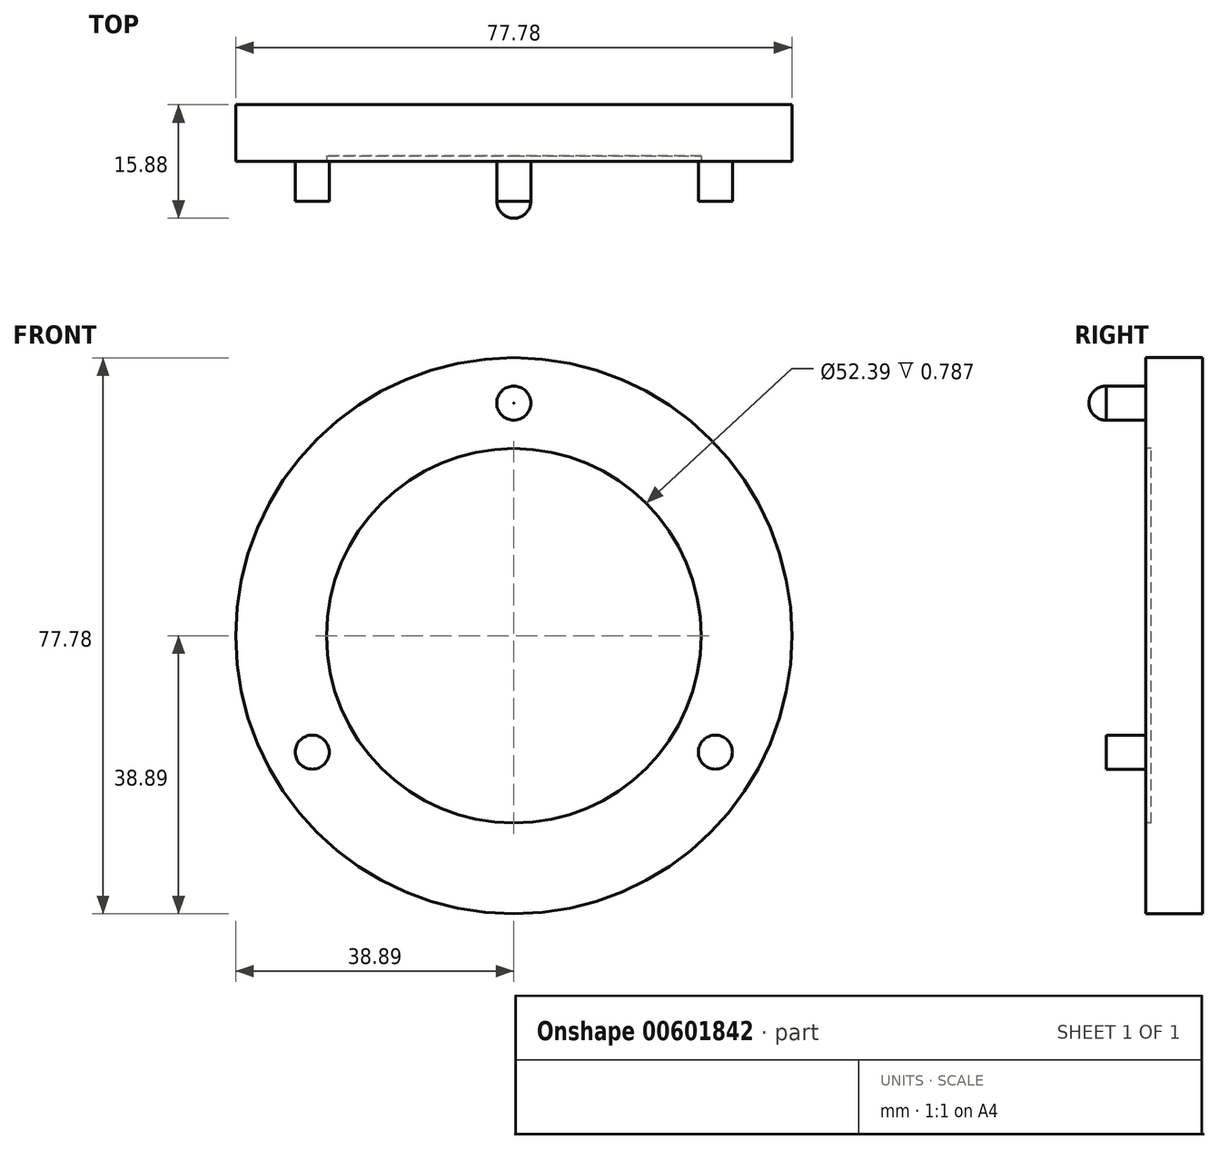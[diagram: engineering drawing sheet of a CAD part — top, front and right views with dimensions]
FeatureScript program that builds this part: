
annotation { "Feature Type Name" : "Feature", "Feature Type Description" : "" }
export const myFeature = defineFeature(function(context is Context, id is Id, definition is map)
    precondition{}
    {
        {
            var Q0;
            Q0=qCreatedBy(makeId("Front.planeOp"),FACE);
            var sketch = newSketch(context, id + "F0", { "sketchPlane" : qUnion([Q0])});
            skCircle(sketch, "E0", {"center": v(0, 0) * mm, "radius": 38.9 * mm});
            skSolve(sketch);
        }
        {
            var Q0;
            Q0=makeQuery(id+"F0.imprint","IMPRINT",FACE,{"disambiguationData":[TD([[makeQuery(id+"F0.imprint","IMPRINT",EDGE,{"derivedFrom":sQuery(id+"F0.wireOp",EDGE,"E0")}),1.0]])]});
            extrude(context, id + "F1", {"entities" : qUnion([Q0]), "depth" : 7.94 * mm, "offsetDistance" : 25.4 * mm});
        }
        {
            var Q0;
            Q0=makeQuery(id+"F1.opExtrude","CAP_FACE",FACE,{"disambiguationData":[OSD([sQuery(id+"F0.wireOp",EDGE,"E0")])],"isStart":false});
            var sketch = newSketch(context, id + "F2", { "sketchPlane" : qUnion([Q0])});
            skCircle(sketch, "E1", {"center": v(0, 0) * mm, "radius": 26.2 * mm});
            skCircle(sketch, "E2", {"center": v(0, 0) * mm, "radius": 38.9 * mm});
            skLineSegment(sketch, "E3", {"start": v(0, 38.9) * mm, "end": v(0, 26.2) * mm, "construction": true});
            skCircle(sketch, "E4", {"center": v(0, 0) * mm, "radius": 32.54 * mm, "construction": true});
            skPoint(sketch, "E5", {"position": v(0, 32.54) * mm});
            skCircle(sketch, "E6", {"center": v(0, 32.54) * mm, "radius": 2.38 * mm});
            skCircle(sketch, "E7.1.0", {"center": v(-28.18, -16.27) * mm, "radius": 2.38 * mm});
            skCircle(sketch, "E7.2.0", {"center": v(28.18, -16.27) * mm, "radius": 2.38 * mm});
            skSolve(sketch);
        }
        {
            var Q0;
            Q0=makeQuery(id+"F2.imprint","IMPRINT",FACE,{"disambiguationData":[TD([[makeQuery(id+"F2.imprint","IMPRINT",EDGE,{"derivedFrom":sQuery(id+"F2.wireOp",EDGE,"E1")}),1.0]])]});
            extrude(context, id + "F3", {"entities" : qUnion([Q0]), "operationType" : NewBodyOperationType.REMOVE, "oppositeDirection" : true, "depth" : 0.79 * mm, "offsetDistance" : 25.4 * mm});
        }
        {
            var Q0;
            Q0=makeQuery(id+"F2.imprint","IMPRINT",FACE,{"disambiguationData":[TD([[makeQuery(id+"F2.imprint","IMPRINT",EDGE,{"derivedFrom":sQuery(id+"F2.wireOp",EDGE,"E6")}),1.0]])]});
            var Q1;
            Q1=makeQuery(id+"F2.imprint","IMPRINT",FACE,{"disambiguationData":[TD([[makeQuery(id+"F2.imprint","IMPRINT",EDGE,{"derivedFrom":sQuery(id+"F2.wireOp",EDGE,"E7.1.0")}),1.0]])]});
            var Q2;
            Q2=makeQuery(id+"F2.imprint","IMPRINT",FACE,{"disambiguationData":[TD([[makeQuery(id+"F2.imprint","IMPRINT",EDGE,{"derivedFrom":sQuery(id+"F2.wireOp",EDGE,"E7.2.0")}),1.0]])]});
            var Q3;
            Q3 = qSketchRegion(id + "FQlptqlQVB5WaVp_2", true);
            extrude(context, id + "F4", {"entities" : qUnion([Q0, Q1, Q2, Q3]), "operationType" : NewBodyOperationType.ADD, "depth" : 5.55 * mm, "offsetDistance" : 25.4 * mm});
        }
        {
            var Q0;
            Q0=qCreatedBy(makeId("Right.planeOp"),FACE);
            var sketch = newSketch(context, id + "F5", { "sketchPlane" : qUnion([Q0])});
            skLineSegment(sketch, "E8.right", {"start": v(-7.94, 34.93) * mm, "end": v(-7.94, 30.16) * mm});
            skLineSegment(sketch, "E9.bottom", {"start": v(-13.49, 34.93) * mm, "end": v(-7.94, 34.93) * mm});
            skLineSegment(sketch, "E9.top", {"start": v(-13.49, 30.16) * mm, "end": v(-7.94, 30.16) * mm});
            skLineSegment(sketch, "E9.left", {"start": v(-13.49, 34.93) * mm, "end": v(-13.49, 30.16) * mm});
            skLineSegment(sketch, "E10", {"start": v(-7.94, 32.54) * mm, "end": v(-15.88, 32.54) * mm});
            skArc(sketch, "E11", {"start": v(-13.49, 34.93) * mm, "mid": v(-15.18, 34.23) * mm, "end": v(-15.88, 32.54) * mm});
            skSolve(sketch);
        }
        {
            var Q0;
            {var subQ0=sQuery(id+"F5.wireOp",EDGE,"E11");Q0=makeQuery(id+"F5.imprint","IMPRINT",FACE,{"disambiguationData":[TD([[makeQuery(id+"F5.imprint","IMPRINT",EDGE,{"derivedFrom":subQ0}),1.0]])]});}
            var Q1;
            Q1=sQuery(id+"F5.wireOp",EDGE,"E10");
            revolve(context, id + "F6", {"operationType" : NewBodyOperationType.ADD, "entities" : qUnion([Q0]), "axis" : qUnion([Q1]), "revolveType" : RevolveType.FULL});
        }
        {
            var Q0;
            Q0=qCreatedBy(makeId("Right.planeOp"),FACE);
            cPlane(context, id + "F7", {"entities" : qUnion([Q0]), "cplaneType" : CPlaneType.OFFSET, "offset" : 28.18 * mm, "width" : 152.4 * mm, "height" : 152.4 * mm});
        }
    });
